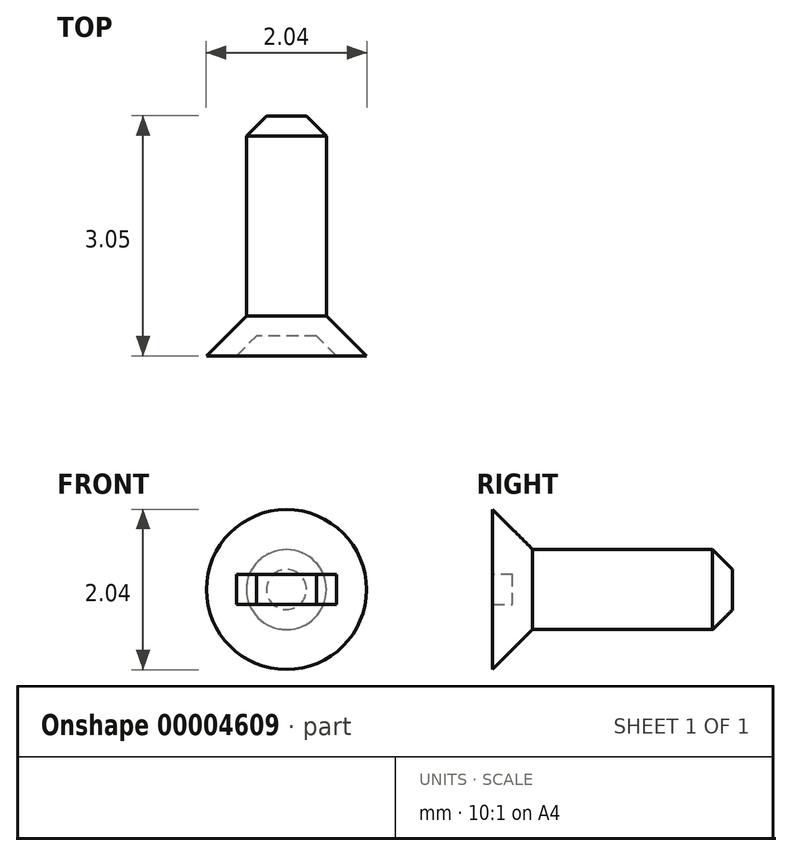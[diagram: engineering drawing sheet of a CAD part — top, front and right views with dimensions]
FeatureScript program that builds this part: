
annotation { "Feature Type Name" : "Feature", "Feature Type Description" : "" }
export const myFeature = defineFeature(function(context is Context, id is Id, definition is map)
    precondition{}
    {
        {
            var Q0;
            Q0=qCreatedBy(makeId("Right.planeOp"),FACE);
            var sketch = newSketch(context, id + "F0", { "sketchPlane" : qUnion([Q0])});
            skLineSegment(sketch, "E0", {"start": v(0, 0) * mm, "end": v(0, 1.02) * mm});
            skLineSegment(sketch, "E1", {"start": v(0, 1.02) * mm, "end": v(0.5, 0.5) * mm});
            skLineSegment(sketch, "E2", {"start": v(0.5, 0.5) * mm, "end": v(3.05, 0.5) * mm});
            skLineSegment(sketch, "E3", {"start": v(3.05, 0.5) * mm, "end": v(3.05, 0) * mm});
            skLineSegment(sketch, "E4", {"start": v(3.05, 0) * mm, "end": v(0, 0) * mm});
            skSolve(sketch);
        }
        {
            var Q0;
            Q0=makeQuery(id+"F0.imprint","IMPRINT",FACE,{"disambiguationData":[TD([[makeQuery(id+"F0.imprint","IMPRINT",EDGE,{"derivedFrom":sQuery(id+"F0.wireOp",EDGE,"E0")}),-1.0]])]});
            var Q1;
            Q1=sQuery(id+"F0.wireOp",EDGE,"E4");
            revolve(context, id + "F1", {"entities" : qUnion([Q0]), "axis" : qUnion([Q1]), "revolveType" : RevolveType.FULL});
        }
        {
            var Q0;
            Q0=makeQuery(id+"F1.opRevolve","SWEPT_EDGE",EDGE,{"disambiguationData":[OSD([sQuery(id+"F0.wireOp",EDGE,"E2"),sQuery(id+"F0.wireOp",EDGE,"E3")])]});
            chamfer(context, id + "F2", {"entities" : qUnion([Q0]), "width" : 0.25 * mm, "tangentPropagation" : true});
        }
        {
            var Q0;
            Q0=makeQuery(id+"F1.opRevolve","SWEPT_FACE",FACE,{"disambiguationData":[OSD([sQuery(id+"F0.wireOp",EDGE,"E0")])]});
            var sketch = newSketch(context, id + "F3", { "sketchPlane" : qUnion([Q0])});
            skLineSegment(sketch, "E5.rect.bottom", {"start": v(0.64, -0.2) * mm, "end": v(-0.64, -0.2) * mm});
            skLineSegment(sketch, "E5.rect.top", {"start": v(0.64, 0.2) * mm, "end": v(-0.64, 0.2) * mm});
            skLineSegment(sketch, "E5.rect.left", {"start": v(0.64, -0.2) * mm, "end": v(0.64, 0.2) * mm});
            skLineSegment(sketch, "E5.rect.right", {"start": v(-0.64, -0.2) * mm, "end": v(-0.64, 0.2) * mm});
            skPoint(sketch, "E5.rect.middle", {"position": v(0, 0) * mm});
            skSolve(sketch);
        }
        {
            var Q0;
            Q0=makeQuery(id+"F3.imprint","IMPRINT",FACE,{"disambiguationData":[TD([[makeQuery(id+"F3.imprint","IMPRINT",EDGE,{"derivedFrom":sQuery(id+"F3.wireOp",EDGE,"E5.rect.bottom")}),-1.0]])]});
            extrude(context, id + "F4", {"entities" : qUnion([Q0]), "operationType" : NewBodyOperationType.REMOVE, "oppositeDirection" : true, "depth" : 0.25 * mm});
        }
        {
            var Q0;
            Q0=makeQuery(id+"F4.boolean.opBoolean","COPY",EDGE,{"derivedFrom":makeQuery(id+"F4.opExtrude","CAP_EDGE",EDGE,{"disambiguationData":[OSD([sQuery(id+"F3.wireOp",EDGE,"E5.rect.left")])],"isStart":false})});
            var Q1;
            Q1=makeQuery(id+"F4.boolean.opBoolean","COPY",EDGE,{"derivedFrom":makeQuery(id+"F4.opExtrude","CAP_EDGE",EDGE,{"disambiguationData":[OSD([sQuery(id+"F3.wireOp",EDGE,"E5.rect.right")])],"isStart":false})});
            chamfer(context, id + "F5", {"entities" : qUnion([Q0, Q1]), "width" : 0.25 * mm, "tangentPropagation" : true});
        }
    });
